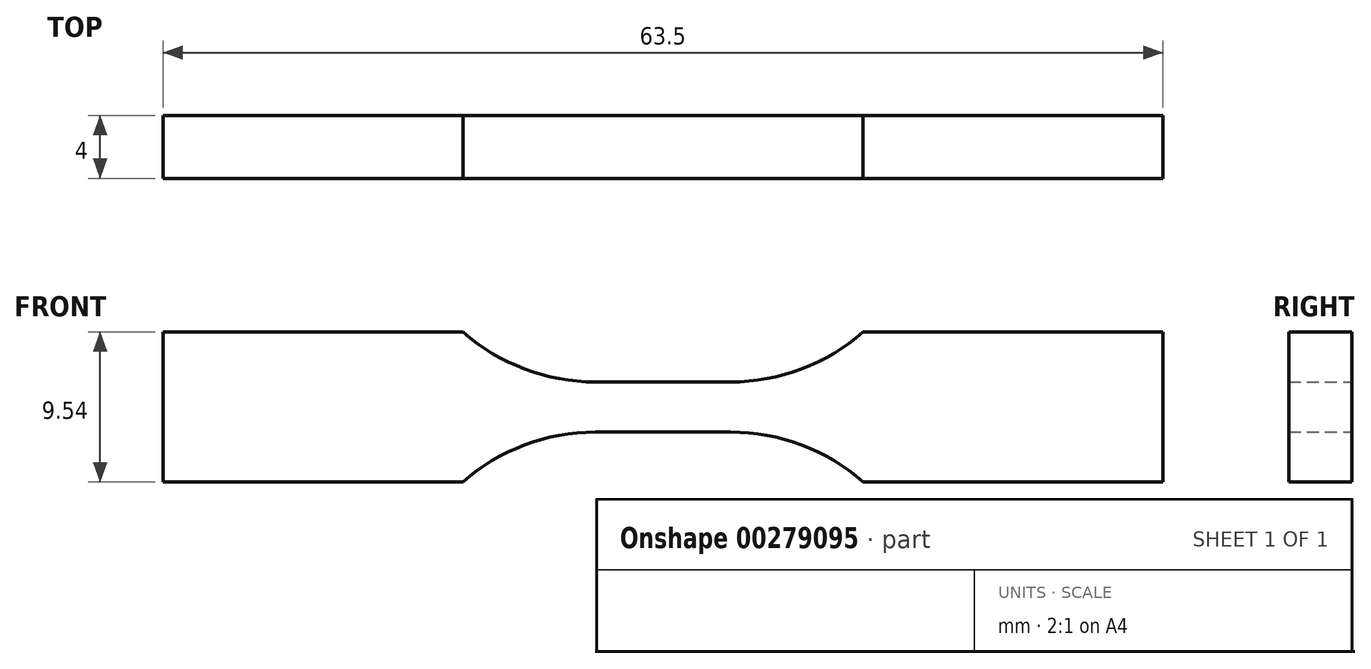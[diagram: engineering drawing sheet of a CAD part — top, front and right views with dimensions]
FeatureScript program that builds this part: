
annotation { "Feature Type Name" : "Feature", "Feature Type Description" : "" }
export const myFeature = defineFeature(function(context is Context, id is Id, definition is map)
    precondition{}
    {
        {
            var Q0;
            Q0=qCreatedBy(makeId("Front.planeOp"),FACE);
            var sketch = newSketch(context, id + "F0", { "sketchPlane" : qUnion([Q0])});
            skLineSegment(sketch, "E0", {"start": v(0, 1.59) * mm, "end": v(4.3, 1.59) * mm});
            skArc(sketch, "E1", {"start": v(4.3, 1.59) * mm, "mid": v(8.79, 2.41) * mm, "end": v(12.7, 4.77) * mm});
            skLineSegment(sketch, "E2", {"start": v(12.7, 4.77) * mm, "end": v(31.75, 4.77) * mm});
            skLineSegment(sketch, "E3.MirrorCS", {"start": v(12.7, -4.76) * mm, "end": v(31.75, -4.76) * mm});
            skLineSegment(sketch, "E4.MirrorCS", {"start": v(0, -1.6) * mm, "end": v(4.3, -1.6) * mm});
            skArc(sketch, "E5.MirrorCS", {"start": v(4.3, -1.59) * mm, "mid": v(8.79, -2.41) * mm, "end": v(12.7, -4.77) * mm});
            skArc(sketch, "E6.MirrorCS", {"start": v(-4.3, -1.59) * mm, "mid": v(-8.79, -2.41) * mm, "end": v(-12.7, -4.77) * mm});
            skLineSegment(sketch, "E7.MirrorCS", {"start": v(0, 1.6) * mm, "end": v(-4.3, 1.6) * mm});
            skArc(sketch, "E8.MirrorCS", {"start": v(-4.3, 1.59) * mm, "mid": v(-8.79, 2.41) * mm, "end": v(-12.7, 4.77) * mm});
            skLineSegment(sketch, "E9.MirrorCS", {"start": v(-12.7, -4.76) * mm, "end": v(-31.75, -4.77) * mm});
            skLineSegment(sketch, "E10.MirrorCS", {"start": v(0, -1.59) * mm, "end": v(-4.3, -1.59) * mm});
            skLineSegment(sketch, "E11.MirrorCS", {"start": v(-12.7, 4.77) * mm, "end": v(-31.75, 4.76) * mm});
            skLineSegment(sketch, "E12", {"start": v(-31.75, 4.77) * mm, "end": v(-31.75, -4.77) * mm});
            skLineSegment(sketch, "E13", {"start": v(31.75, 4.77) * mm, "end": v(31.75, -4.77) * mm});
            skSolve(sketch);
        }
        {
            var Q0;
            Q0=makeQuery(id+"F0.imprint","IMPRINT",FACE,{"disambiguationData":[TD([[makeQuery(id+"F0.imprint","IMPRINT",EDGE,{"derivedFrom":sQuery(id+"F0.wireOp",EDGE,"E0")}),-1.0]])]});
            extrude(context, id + "F1", {"entities" : qUnion([Q0]), "endBound" : BoundingType.SYMMETRIC, "depth" : 4 * mm});
        }
    });
